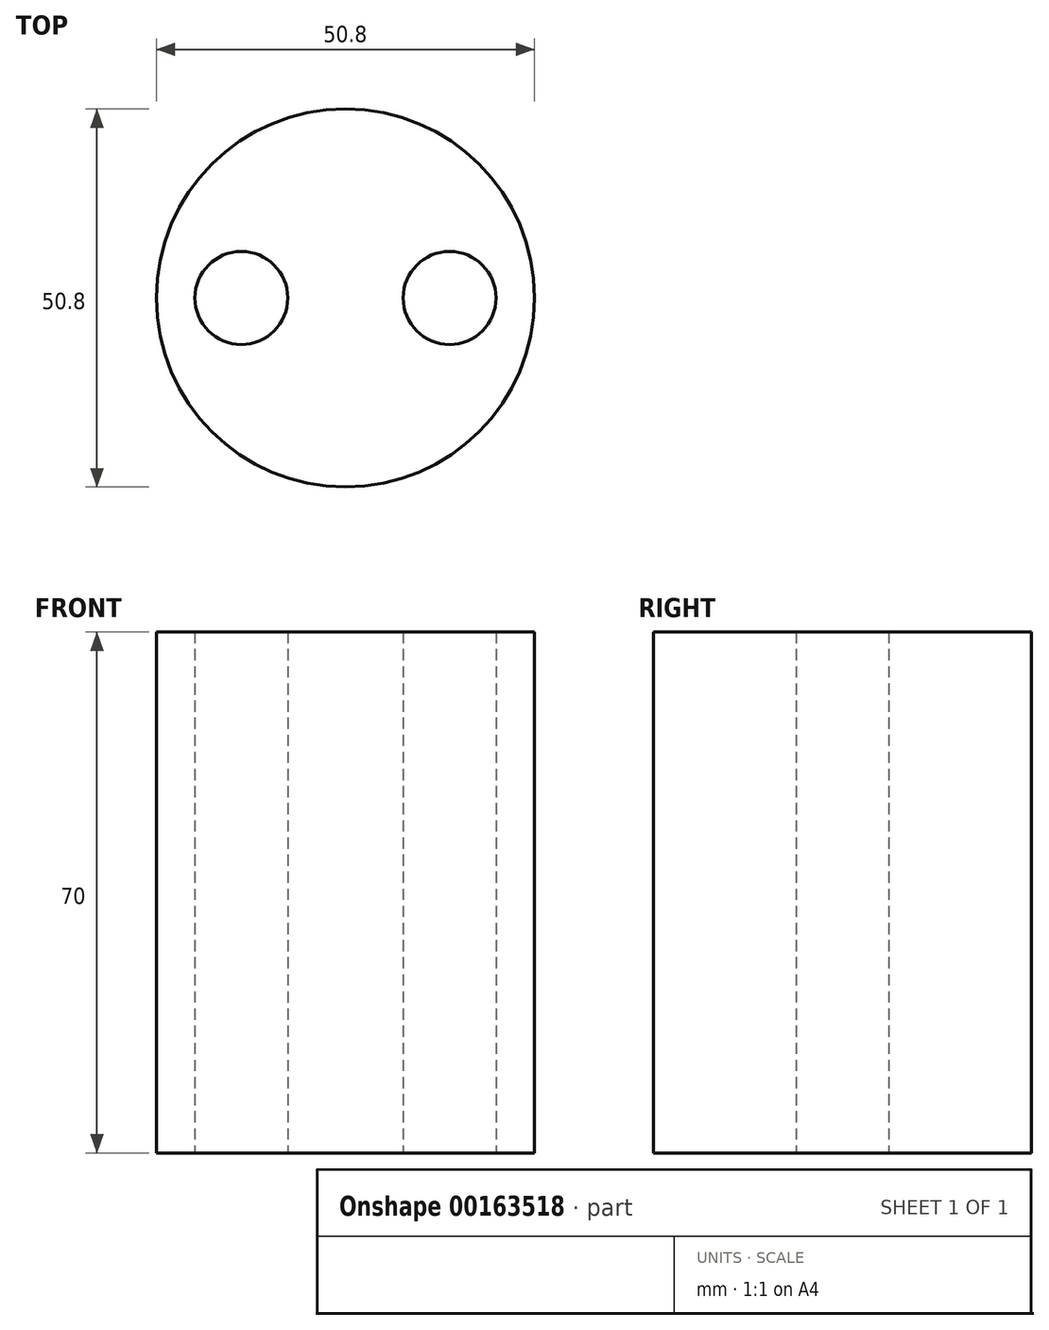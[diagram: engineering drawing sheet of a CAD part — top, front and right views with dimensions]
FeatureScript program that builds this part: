
annotation { "Feature Type Name" : "Feature", "Feature Type Description" : "" }
export const myFeature = defineFeature(function(context is Context, id is Id, definition is map)
    precondition{}
    {
        {
            var Q0;
            Q0=qCreatedBy(makeId("Top.planeOp"),FACE);
            var sketch = newSketch(context, id + "F0", { "sketchPlane" : qUnion([Q0])});
            skCircle(sketch, "E0", {"center": v(0, 0) * mm, "radius": 25.4 * mm});
            skCircle(sketch, "E1", {"center": v(14, 0) * mm, "radius": 6.25 * mm});
            skCircle(sketch, "E2", {"center": v(-14, 0) * mm, "radius": 6.25 * mm});
            skSolve(sketch);
        }
        {
            var Q0;
            Q0 = qSketchRegion(id + "F0", true);
            extrude(context, id + "F1", {"entities" : qUnion([Q0]), "depth" : 70 * mm});
        }
    });
